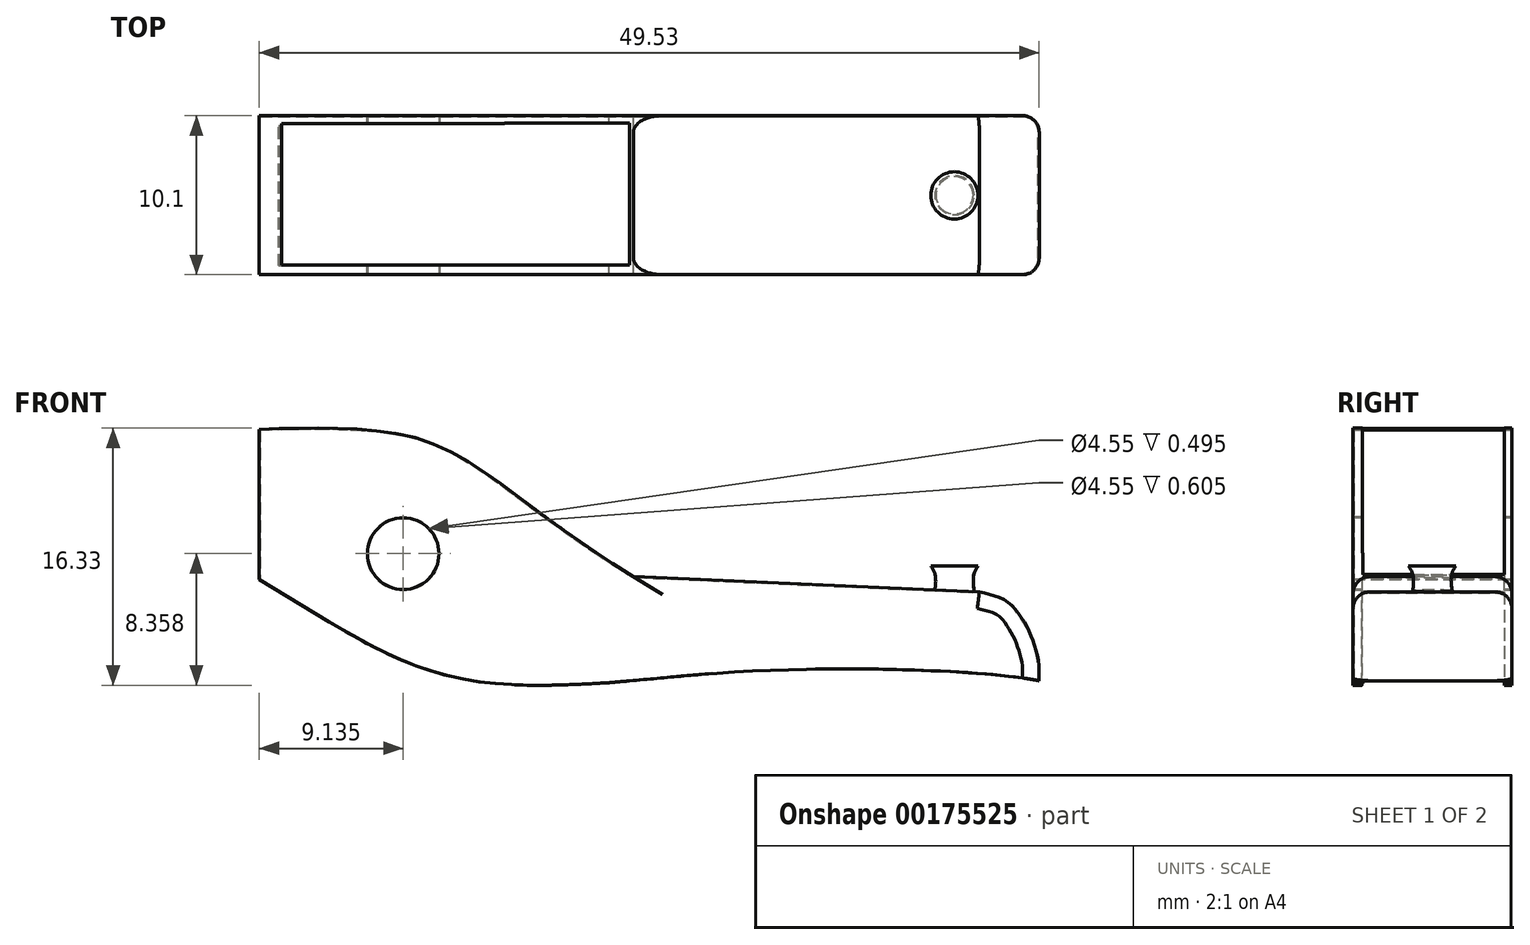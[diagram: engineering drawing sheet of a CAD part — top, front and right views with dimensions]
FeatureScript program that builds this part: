
annotation { "Feature Type Name" : "Feature", "Feature Type Description" : "" }
export const myFeature = defineFeature(function(context is Context, id is Id, definition is map)
    precondition{}
    {
        {
            var Q0;
            Q0=qCreatedBy(makeId("Front.planeOp"),FACE);
            var sketch = newSketch(context, id + "F0", { "sketchPlane" : qUnion([Q0])});
            skLineSegment(sketch, "E0", {"start": v(-18.11, 14.62) * mm, "end": v(-18.11, 5.15) * mm});
            skFitSpline(sketch, "E1", {"points": [v(-18.11, 14.62) * mm, v(-5.7, 13.04) * mm, v(5.6, 5.26) * mm], "startDerivative": vector(43.3, 1.46) * mm, "endDerivative": vector(32.79, -20.12) * mm});
            skFitSpline(sketch, "E2", {"points": [v(-18.11, 5.15) * mm, v(-6.1, -0.96) * mm, v(5.6, -1.29) * mm], "startDerivative": vector(24.76, -14.65) * mm, "endDerivative": vector(22.2, 1.12) * mm});
            skLineSegment(sketch, "E3", {"start": v(-5.7, 13.04) * mm, "end": v(-6.1, -0.96) * mm, "construction": true});
            skFitSpline(sketch, "E4", {"points": [v(5.6, -1.29) * mm, v(15.63, -0.6) * mm, v(31.3, -1.29) * mm], "startDerivative": vector(20.89, 1.84) * mm, "endDerivative": vector(17.9, -3.47) * mm});
            skLineSegment(sketch, "E5", {"start": v(5.6, 5.26) * mm, "end": v(27.57, 4.28) * mm});
            skFitSpline(sketch, "E6", {"points": [v(27.57, 4.28) * mm, v(29.94, 3.06) * mm, v(31.3, -1.29) * mm], "startDerivative": vector(9.56, -2.1) * mm, "endDerivative": vector(-1.08, -8.77) * mm});
            skLineSegment(sketch, "E7", {"start": v(-18.11, 14.62) * mm, "end": v(31.89, 14.62) * mm, "construction": true});
            skLineSegment(sketch, "E8", {"start": v(31.89, 14.62) * mm, "end": v(31.3, -1.29) * mm, "construction": true});
            skSolve(sketch);
        }
        {
            var Q0;
            Q0=qSketchRegion(id+"F0",true);
            extrude(context, id + "F1", {"entities" : qUnion([Q0]), "depth" : 10 * mm});
        }
        {
            var Q0;
            Q0=makeQuery(id+"F1.opExtrude","CAP_FACE",FACE,{"disambiguationData":[OSD([sQuery(id+"F0.wireOp",EDGE,"E0"),sQuery(id+"F0.wireOp",EDGE,"E1"),sQuery(id+"F0.wireOp",EDGE,"E2"),sQuery(id+"F0.wireOp",EDGE,"E4"),sQuery(id+"F0.wireOp",EDGE,"E5"),sQuery(id+"F0.wireOp",EDGE,"E6")])],"isStart":false});
            var sketch = newSketch(context, id + "F2", { "sketchPlane" : qUnion([Q0])});
            skCircle(sketch, "E9", {"center": v(-9.02, 6.77) * mm, "radius": 2.32 * mm});
            skSolve(sketch);
        }
        {
            var Q0;
            Q0=qSketchRegion(id+"F2",true);
            extrude(context, id + "F3", {"entities" : qUnion([Q0]), "operationType" : NewBodyOperationType.REMOVE, "oppositeDirection" : true, "depth" : 25 * mm});
        }
        {
            var Q0;
            Q0=makeQuery(id+"F1.opExtrude","CAP_EDGE",EDGE,{"disambiguationData":[OSD([sQuery(id+"F0.wireOp",EDGE,"E5")])],"isStart":false});
            var Q1;
            Q1=makeQuery(id+"F1.opExtrude","CAP_EDGE",EDGE,{"disambiguationData":[OSD([sQuery(id+"F0.wireOp",EDGE,"E5")])],"isStart":true});
            var Q2;
            Q2=makeQuery(id+"F1.opExtrude","CAP_EDGE",EDGE,{"disambiguationData":[OSD([sQuery(id+"F0.wireOp",EDGE,"E6")])],"isStart":false});
            var Q3;
            Q3=makeQuery(id+"F1.opExtrude","CAP_EDGE",EDGE,{"disambiguationData":[OSD([sQuery(id+"F0.wireOp",EDGE,"E6")])],"isStart":true});
            fillet(context, id + "F4", {"entities" : qUnion([Q0, Q1, Q2, Q3]), "radius" : 1 * mm, "tangentPropagation" : true, "allowEdgeOverflow" : false});
        }
        {
            var Q0;
            Q0=makeQuery(id+"F1.opExtrude","SWEPT_FACE",FACE,{"disambiguationData":[OSD([sQuery(id+"F0.wireOp",EDGE,"E4")])]});
            shell(context, id + "F5", {"entities" : qUnion([Q0]), "thickness" : 0.05 * mm, "oppositeDirection" : true});
        }
        {
            var Q0;
            Q0=qCreatedBy(makeId("Top.planeOp"),FACE);
            cPlane(context, id + "F6", {"entities" : qUnion([Q0]), "cplaneType" : CPlaneType.OFFSET, "offset" : 16 * mm, "width" : 150 * mm, "height" : 150 * mm});
        }
        {
            var Q0;
            Q0=qCreatedBy(id+"F6.planeOp",FACE);
            var sketch = newSketch(context, id + "F7", { "sketchPlane" : qUnion([Q0])});
            skLineSegment(sketch, "E10.bottom", {"start": v(-16.76, -0.44) * mm, "end": v(3.24, -0.44) * mm});
            skLineSegment(sketch, "E10.top", {"start": v(-16.76, -9.44) * mm, "end": v(3.24, -9.44) * mm});
            skLineSegment(sketch, "E10.left", {"start": v(-16.76, -0.44) * mm, "end": v(-16.76, -9.44) * mm});
            skLineSegment(sketch, "E10.right", {"start": v(3.24, -0.44) * mm, "end": v(3.24, -9.44) * mm});
            skPoint(sketch, "E10.middle", {"position": v(-6.76, -4.94) * mm});
            skSolve(sketch);
        }
        {
            var Q0;
            Q0=qSketchRegion(id+"F7",true);
            extrude(context, id + "F8", {"entities" : qUnion([Q0]), "operationType" : NewBodyOperationType.REMOVE, "oppositeDirection" : true, "depth" : 20 * mm});
        }
        {
            var Q0;
            Q0=qCreatedBy(makeId("Top.planeOp"),FACE);
            cPlane(context, id + "F9", {"entities" : qUnion([Q0]), "cplaneType" : CPlaneType.OFFSET, "offset" : 3 * mm, "oppositeDirection" : true, "width" : 150 * mm, "height" : 150 * mm});
        }
        {
            var Q0;
            Q0=qCreatedBy(id+"F9.planeOp",FACE);
            var sketch = newSketch(context, id + "F10", { "sketchPlane" : qUnion([Q0])});
            skLineSegment(sketch, "E11.bottom", {"start": v(-17.45, -0.6) * mm, "end": v(3.47, -0.6) * mm});
            skLineSegment(sketch, "E11.top", {"start": v(-17.45, -9.48) * mm, "end": v(3.47, -9.48) * mm});
            skLineSegment(sketch, "E11.left", {"start": v(-17.45, -0.6) * mm, "end": v(-17.45, -9.48) * mm});
            skLineSegment(sketch, "E11.right", {"start": v(3.47, -0.6) * mm, "end": v(3.47, -9.48) * mm});
            skPoint(sketch, "E11.middle", {"position": v(-7, -5.04) * mm});
            skSolve(sketch);
        }
        {
            var Q0;
            Q0=qSketchRegion(id+"F10",true);
            extrude(context, id + "F11", {"entities" : qUnion([Q0]), "operationType" : NewBodyOperationType.REMOVE, "depth" : 7.4 * mm});
        }
        {
            var Q0;
            Q0=qCreatedBy(id+"F6.planeOp",FACE);
            var sketch = newSketch(context, id + "F12", { "sketchPlane" : qUnion([Q0])});
            skLineSegment(sketch, "E12.bottom", {"start": v(-2.58, -0.44) * mm, "end": v(5.36, -0.44) * mm});
            skLineSegment(sketch, "E12.top", {"start": v(-2.58, -9.44) * mm, "end": v(5.36, -9.44) * mm});
            skLineSegment(sketch, "E12.left", {"start": v(-2.58, -0.44) * mm, "end": v(-2.58, -9.44) * mm});
            skLineSegment(sketch, "E12.right", {"start": v(5.36, -0.44) * mm, "end": v(5.36, -9.44) * mm});
            skSolve(sketch);
        }
        {
            var Q0;
            Q0=qSketchRegion(id+"F12",true);
            extrude(context, id + "F13", {"entities" : qUnion([Q0]), "operationType" : NewBodyOperationType.REMOVE, "oppositeDirection" : true, "depth" : 50 * mm});
        }
        {
            var Q0;
            Q0=makeQuery(id+"F1.opExtrude","SWEPT_FACE",FACE,{"disambiguationData":[OSD([sQuery(id+"F0.wireOp",EDGE,"E5")])]});
            var sketch = newSketch(context, id + "F14", { "sketchPlane" : qUnion([Q0])});
            skCircle(sketch, "E13", {"center": v(25.77, -5) * mm, "radius": 1.25 * mm});
            skLineSegment(sketch, "E14", {"start": v(31.27, 0) * mm, "end": v(31.27, -10.1) * mm, "construction": true});
            skLineSegment(sketch, "E15", {"start": v(7.93, 0) * mm, "end": v(31.27, 0) * mm, "construction": true});
            skSolve(sketch);
        }
        {
            var Q0;
            Q0=qCreatedBy(makeId("Top.planeOp"),FACE);
            cPlane(context, id + "F15", {"entities" : qUnion([Q0]), "cplaneType" : CPlaneType.OFFSET, "offset" : 5.5 * mm, "width" : 150 * mm, "height" : 150 * mm});
        }
        {
            var Q0;
            Q0=qCreatedBy(id+"F15.planeOp",FACE);
            cPlane(context, id + "F16", {"entities" : qUnion([Q0]), "cplaneType" : CPlaneType.OFFSET, "offset" : 0.5 * mm, "width" : 150 * mm, "height" : 150 * mm});
        }
        {
            var Q0;
            Q0=qCreatedBy(id+"F15.planeOp",FACE);
            var sketch = newSketch(context, id + "F17", { "sketchPlane" : qUnion([Q0])});
            skCircle(sketch, "E16", {"center": v(25.99, -5.02) * mm, "radius": 1.25 * mm});
            skSolve(sketch);
        }
        {
            var Q0;
            Q0=qCreatedBy(id+"F16.planeOp",FACE);
            var sketch = newSketch(context, id + "F18", { "sketchPlane" : qUnion([Q0])});
            skCircle(sketch, "E17", {"center": v(25.99, -5.02) * mm, "radius": 1.5 * mm});
            skSolve(sketch);
        }
        {
            var Q1;
            Q1=qSketchRegion(id+"F14",true);
            var Q2;
            Q2=qSketchRegion(id+"F17",true);
            var Q3;
            Q3=qSketchRegion(id+"F18",true);
            loft(context, id + "F19", {"operationType" : NewBodyOperationType.ADD, "sheetProfilesArray" : [{ "sheetProfileEntities" : qUnion([Q1]) }, { "sheetProfileEntities" : qUnion([Q2]) }, { "sheetProfileEntities" : qUnion([Q3]) }]});
        }
    });
